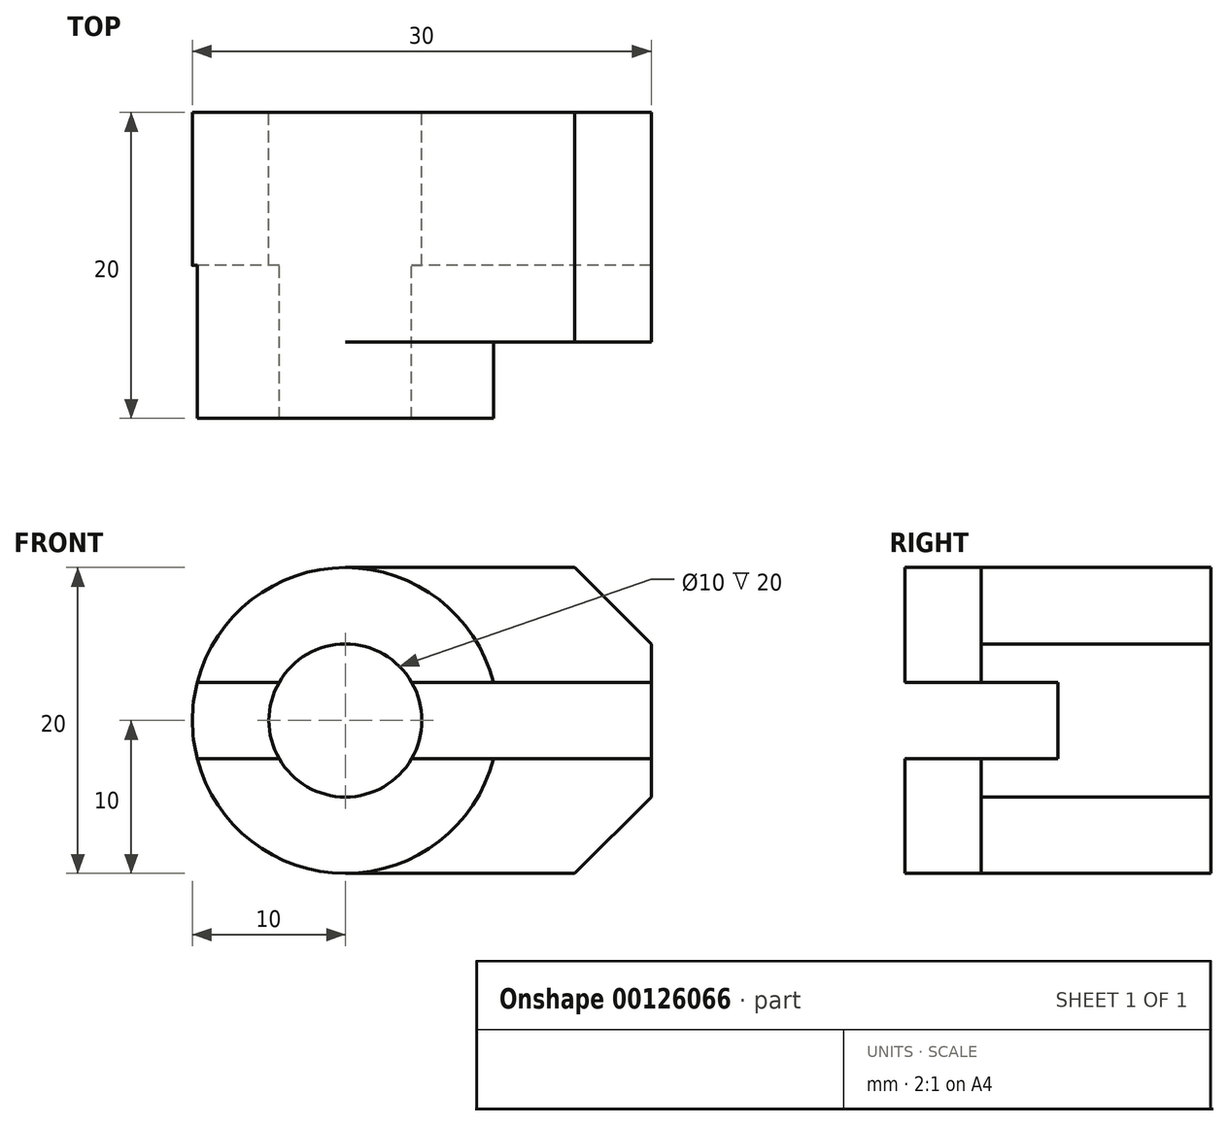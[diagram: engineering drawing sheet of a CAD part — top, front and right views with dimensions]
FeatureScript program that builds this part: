
annotation { "Feature Type Name" : "Feature", "Feature Type Description" : "" }
export const myFeature = defineFeature(function(context is Context, id is Id, definition is map)
    precondition{}
    {
        {
            var Q0;
            Q0=qCreatedBy(makeId("Front.planeOp"),FACE);
            var sketch = newSketch(context, id + "F0", { "sketchPlane" : qUnion([Q0])});
            skCircle(sketch, "E0", {"center": v(0, 0) * mm, "radius": 10 * mm});
            skCircle(sketch, "E1", {"center": v(0, 0) * mm, "radius": 5 * mm});
            skLineSegment(sketch, "E2", {"start": v(0, -10) * mm, "end": v(15, -10) * mm});
            skLineSegment(sketch, "E3", {"start": v(-26.83, 0) * mm, "end": v(-33.58, 0) * mm, "construction": true});
            skLineSegment(sketch, "E4.MirrorCS", {"start": v(0, 10) * mm, "end": v(15, 10) * mm});
            skLineSegment(sketch, "E5", {"start": v(15, -10) * mm, "end": v(20, -5) * mm});
            skLineSegment(sketch, "E6", {"start": v(15, -10) * mm, "end": v(22.63, -10) * mm, "construction": true});
            skLineSegment(sketch, "E7", {"start": v(20, -5) * mm, "end": v(20, 0) * mm});
            skLineSegment(sketch, "E8.MirrorCS", {"start": v(15, 10) * mm, "end": v(20, 5) * mm});
            skLineSegment(sketch, "E9.MirrorCS", {"start": v(20, 5) * mm, "end": v(20, 0) * mm});
            skLineSegment(sketch, "E10", {"start": v(20, 2.5) * mm, "end": v(4.33, 2.5) * mm});
            skLineSegment(sketch, "E11", {"start": v(-4.33, 2.5) * mm, "end": v(-9.68, 2.5) * mm});
            skLineSegment(sketch, "E12.MirrorCS", {"start": v(-4.33, -2.5) * mm, "end": v(-9.68, -2.5) * mm});
            skLineSegment(sketch, "E13.MirrorCS", {"start": v(20, -2.5) * mm, "end": v(4.33, -2.5) * mm});
            skSolve(sketch);
        }
        {
            var Q0;
            {var subQ5=sQuery(id+"F0.wireOp",EDGE,"E11");Q0=makeQuery(id+"F0.imprint","IMPRINT",FACE,{"disambiguationData":[TD([[makeQuery(id+"F0.imprint","IMPRINT",EDGE,{"derivedFrom":subQ5}),-1.0]])]});}
            var Q1;
            {var subQ0=sQuery(id+"F0.wireOp",EDGE,"E12.MirrorCS");Q1=makeQuery(id+"F0.imprint","IMPRINT",FACE,{"disambiguationData":[TD([[makeQuery(id+"F0.imprint","IMPRINT",EDGE,{"derivedFrom":subQ0}),1.0]])]});}
            extrude(context, id + "F1", {"entities" : qUnion([Q0, Q1]), "depth" : 20 * mm});
        }
        {
            var Q0;
            {var subQ0=sQuery(id+"F0.wireOp",EDGE,"E10");var subQ3=sQuery(id+"F0.wireOp",EDGE,"E0");var subQ4=makeQuery(id+"F0.imprint","INTERSECT",VERTEX,{"derivedFrom":[subQ3,subQ0]});Q0=makeQuery(id+"F0.imprint","IMPRINT",FACE,{"disambiguationData":[TD([[makeQuery(id+"F0.imprint","IMPRINT",EDGE,{"disambiguationData":[TD([[subQ4,1.0]])],"derivedFrom":subQ3}),-1.0]])]});}
            var Q1;
            {var subQ0=sQuery(id+"F0.wireOp",EDGE,"E10");var subQ1=sQuery(id+"F0.wireOp",EDGE,"E0");var subQ2=makeQuery(id+"F0.imprint","INTERSECT",VERTEX,{"derivedFrom":[subQ1,subQ0]});Q1=makeQuery(id+"F0.imprint","IMPRINT",FACE,{"disambiguationData":[TD([[makeQuery(id+"F0.imprint","IMPRINT",EDGE,{"disambiguationData":[TD([[subQ2,1.0]])],"derivedFrom":subQ1}),1.0]])]});}
            var Q2;
            {var subQ0=sQuery(id+"F0.wireOp",EDGE,"E11");Q2=makeQuery(id+"F0.imprint","IMPRINT",FACE,{"disambiguationData":[TD([[makeQuery(id+"F0.imprint","IMPRINT",EDGE,{"derivedFrom":subQ0}),1.0]])]});}
            extrude(context, id + "F2", {"entities" : qUnion([Q0, Q1, Q2]), "operationType" : NewBodyOperationType.ADD, "depth" : 10 * mm});
        }
        {
            var Q0;
            {var subQ1=sQuery(id+"F0.wireOp",EDGE,"E4.MirrorCS");Q0=makeQuery(id+"F0.imprint","IMPRINT",FACE,{"disambiguationData":[TD([[makeQuery(id+"F0.imprint","IMPRINT",EDGE,{"derivedFrom":subQ1}),-1.0]])]});}
            var Q1;
            {var subQ4=sQuery(id+"F0.wireOp",EDGE,"E2");Q1=makeQuery(id+"F0.imprint","IMPRINT",FACE,{"disambiguationData":[TD([[makeQuery(id+"F0.imprint","IMPRINT",EDGE,{"derivedFrom":subQ4}),1.0]])]});}
            extrude(context, id + "F3", {"entities" : qUnion([Q0, Q1]), "operationType" : NewBodyOperationType.ADD, "depth" : 15 * mm});
        }
    });
